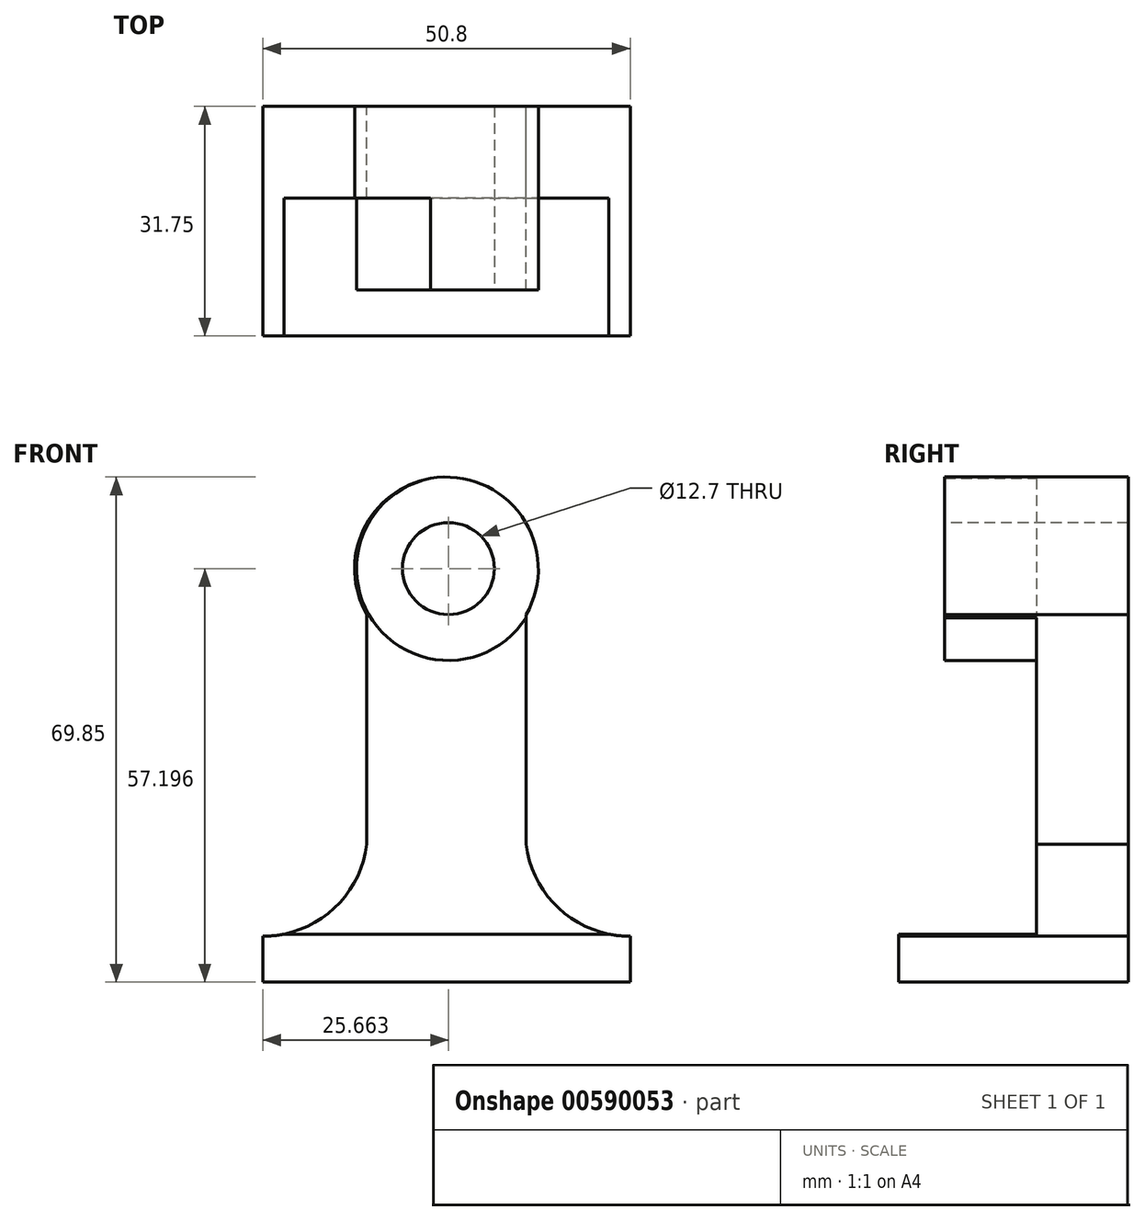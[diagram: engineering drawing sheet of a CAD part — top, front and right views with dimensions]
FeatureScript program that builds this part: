
annotation { "Feature Type Name" : "Feature", "Feature Type Description" : "" }
export const myFeature = defineFeature(function(context is Context, id is Id, definition is map)
    precondition{}
    {
        {
            var Q0;
            Q0=qCreatedBy(makeId("Front.planeOp"),FACE);
            var sketch = newSketch(context, id + "F0", { "sketchPlane" : qUnion([Q0])});
            skLineSegment(sketch, "E0", {"start": v(-10.32, 26.3) * mm, "end": v(-10.32, -43.55) * mm});
            skLineSegment(sketch, "E1", {"start": v(-10.32, -43.55) * mm, "end": v(40.48, -43.55) * mm});
            skLineSegment(sketch, "E2", {"start": v(40.48, -43.55) * mm, "end": v(40.48, 26.3) * mm});
            skLineSegment(sketch, "E3", {"start": v(40.48, 26.3) * mm, "end": v(-10.32, 26.3) * mm});
            skCircle(sketch, "E4", {"center": v(15.08, 13.6) * mm, "radius": 12.7 * mm});
            skLineSegment(sketch, "E5", {"start": v(-10.32, -37.2) * mm, "end": v(40.48, -37.2) * mm});
            skLineSegment(sketch, "E6", {"start": v(26.08, 7.25) * mm, "end": v(26.08, -37.2) * mm});
            skLineSegment(sketch, "E7", {"start": v(4.08, 7.25) * mm, "end": v(4.08, -37.2) * mm});
            skArc(sketch, "E8", {"start": v(26.08, -24.5) * mm, "mid": v(30.88, -33.57) * mm, "end": v(40.48, -37.2) * mm});
            skArc(sketch, "E9", {"start": v(-10.32, -37.2) * mm, "mid": v(-0.72, -33.57) * mm, "end": v(4.08, -24.5) * mm});
            skSolve(sketch);
        }
        {
            var Q0;
            {var subQ0=sQuery(id+"F0.wireOp",EDGE,"E4");var subQ1=makeQuery(id+"F0.imprint","INTERSECT",VERTEX,{"derivedFrom":[subQ0,sQuery(id+"F0.wireOp",EDGE,"E7")]});Q0=makeQuery(id+"F0.imprint","IMPRINT",FACE,{"disambiguationData":[TD([[makeQuery(id+"F0.imprint","IMPRINT",EDGE,{"disambiguationData":[TD([[subQ1,1.0]])],"derivedFrom":subQ0}),1.0]])]});}
            var Q1;
            {var subQ0=sQuery(id+"F0.wireOp",EDGE,"E6");var subQ6=sQuery(id+"F0.wireOp",EDGE,"E4");var subQ7=makeQuery(id+"F0.imprint","INTERSECT",VERTEX,{"derivedFrom":[subQ6,subQ0]});Q1=makeQuery(id+"F0.imprint","IMPRINT",FACE,{"disambiguationData":[TD([[makeQuery(id+"F0.imprint","IMPRINT",EDGE,{"disambiguationData":[TD([[subQ7,1.0]])],"derivedFrom":subQ6}),-1.0]])]});}
            var Q2;
            {var subQ0=sQuery(id+"F0.wireOp",EDGE,"E8");Q2=makeQuery(id+"F0.imprint","IMPRINT",FACE,{"disambiguationData":[TD([[makeQuery(id+"F0.imprint","IMPRINT",EDGE,{"derivedFrom":subQ0}),-1.0]])]});}
            var Q3;
            {var subQ0=sQuery(id+"F0.wireOp",EDGE,"E9");Q3=makeQuery(id+"F0.imprint","IMPRINT",FACE,{"disambiguationData":[TD([[makeQuery(id+"F0.imprint","IMPRINT",EDGE,{"derivedFrom":subQ0}),-1.0]])]});}
            var Q4;
            {var subQ5=sQuery(id+"F0.wireOp",EDGE,"E1");Q4=makeQuery(id+"F0.imprint","IMPRINT",FACE,{"disambiguationData":[TD([[makeQuery(id+"F0.imprint","IMPRINT",EDGE,{"derivedFrom":subQ5}),1.0]])]});}
            extrude(context, id + "F1", {"entities" : qUnion([Q0, Q1, Q2, Q3, Q4]), "depth" : 12.7 * mm, "offsetDistance" : 25.4 * mm});
        }
        {
            var Q0;
            Q0=makeQuery(id+"F1.opExtrude","CAP_FACE",FACE,{"disambiguationData":[OSD([sQuery(id+"F0.wireOp",EDGE,"E0"),sQuery(id+"F0.wireOp",EDGE,"E1"),sQuery(id+"F0.wireOp",EDGE,"E2"),sQuery(id+"F0.wireOp",EDGE,"E4"),sQuery(id+"F0.wireOp",EDGE,"E6"),sQuery(id+"F0.wireOp",EDGE,"E7"),sQuery(id+"F0.wireOp",EDGE,"E8"),sQuery(id+"F0.wireOp",EDGE,"E9")])],"isStart":false});
            var sketch = newSketch(context, id + "F2", { "sketchPlane" : qUnion([Q0])});
            skSolve(sketch);
        }
        {
            var Q0;
            Q0=makeQuery(id+"F2.imprint","IMPRINT",FACE,{"disambiguationData":[TD([[makeQuery(id+"F2.imprint","IMPRINT",EDGE,{"derivedFrom":makeQuery(id+"F1.opExtrude","CAP_EDGE",EDGE,{"disambiguationData":[OSD([sQuery(id+"F0.wireOp",EDGE,"E0")])],"isStart":false})}),1.0]])]});
            var sketch = newSketch(context, id + "F3", { "sketchPlane" : qUnion([Q0])});
            skLineSegment(sketch, "E10", {"start": v(40.34, -36.9) * mm, "end": v(-10.05, -36.9) * mm});
            skSolve(sketch);
        }
        {
            var Q0;
            {var subQ1=makeQuery(id+"F2.imprint","IMPRINT",EDGE,{"derivedFrom":makeQuery(id+"F1.opExtrude","CAP_EDGE",EDGE,{"disambiguationData":[OSD([sQuery(id+"F0.wireOp",EDGE,"E0")])],"isStart":false})});Q0=makeQuery(id+"F3.imprint","IMPRINT",FACE,{"disambiguationData":[TD([[makeQuery(id+"F3.imprint","IMPRINT",EDGE,{"derivedFrom":subQ1}),1.0]])]});}
            extrude(context, id + "F4", {"entities" : qUnion([Q0]), "operationType" : NewBodyOperationType.ADD, "depth" : 19.05 * mm, "offsetDistance" : 25.4 * mm});
        }
        {
            var Q0;
            Q0=makeQuery(id+"F2.imprint","IMPRINT",FACE,{"disambiguationData":[TD([[makeQuery(id+"F2.imprint","IMPRINT",EDGE,{"derivedFrom":makeQuery(id+"F1.opExtrude","CAP_EDGE",EDGE,{"disambiguationData":[OSD([sQuery(id+"F0.wireOp",EDGE,"E0")])],"isStart":false})}),1.0]])]});
            var sketch = newSketch(context, id + "F5", { "sketchPlane" : qUnion([Q0])});
            skCircle(sketch, "E11", {"center": v(15.34, 13.65) * mm, "radius": 12.7 * mm});
            skSolve(sketch);
        }
        {
            var Q0;
            {var subQ0=sQuery(id+"F5.wireOp",EDGE,"E11");var subQ1=makeQuery(id+"F2.imprint","IMPRINT",EDGE,{"derivedFrom":makeQuery(id+"F1.opExtrude","CAP_EDGE",EDGE,{"disambiguationData":[OSD([sQuery(id+"F0.wireOp",EDGE,"E4")])],"isStart":false})});var subQ2=makeQuery(id+"F5.imprint","INTERSECT",VERTEX,{"derivedFrom":[subQ1,subQ0]});Q0=makeQuery(id+"F5.imprint","IMPRINT",FACE,{"disambiguationData":[TD([[makeQuery(id+"F5.imprint","IMPRINT",EDGE,{"disambiguationData":[TD([[subQ2,-1.0]])],"derivedFrom":subQ0}),1.0]])]});}
            extrude(context, id + "F6", {"entities" : qUnion([Q0]), "operationType" : NewBodyOperationType.ADD, "depth" : 12.7 * mm, "offsetDistance" : 25.4 * mm});
        }
        {
            var Q0;
            Q0=makeQuery(id+"F6.opExtrude","CAP_FACE",FACE,{"disambiguationData":[OSD([sQuery(id+"F0.wireOp",EDGE,"E4"),sQuery(id+"F0.wireOp",EDGE,"E6"),sQuery(id+"F5.wireOp",EDGE,"E11")])],"isStart":false});
            var sketch = newSketch(context, id + "F7", { "sketchPlane" : qUnion([Q0])});
            skCircle(sketch, "E12", {"center": v(15.34, 13.65) * mm, "radius": 6.35 * mm});
            skSolve(sketch);
        }
        {
            var Q0;
            Q0 = qSketchRegion(id + "F7", true);
            extrude(context, id + "F8", {"entities" : qUnion([Q0]), "operationType" : NewBodyOperationType.REMOVE, "oppositeDirection" : true, "depth" : 110.49 * mm, "offsetDistance" : 25.4 * mm});
        }
    });
